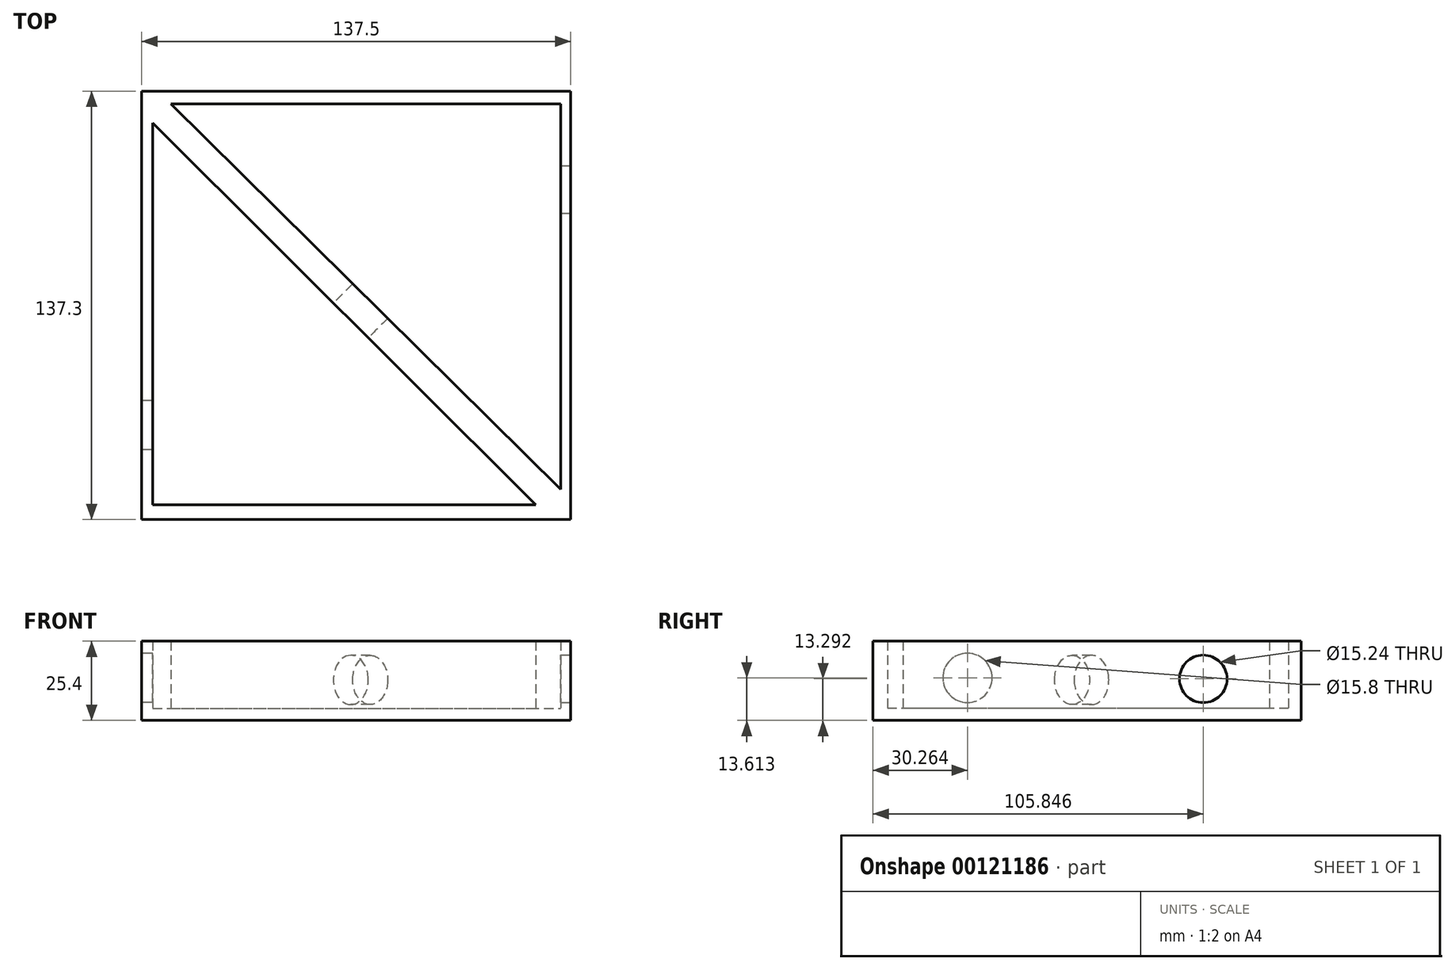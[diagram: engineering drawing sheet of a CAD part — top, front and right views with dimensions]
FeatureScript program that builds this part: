
annotation { "Feature Type Name" : "Feature", "Feature Type Description" : "" }
export const myFeature = defineFeature(function(context is Context, id is Id, definition is map)
    precondition{}
    {
        {
            var Q0;
            Q0=qCreatedBy(makeId("Top.planeOp"),FACE);
            var sketch = newSketch(context, id + "F0", { "sketchPlane" : qUnion([Q0])});
            skLineSegment(sketch, "E0.bottom", {"start": v(-66.4, 69.43) * mm, "end": v(71.1, 69.43) * mm});
            skLineSegment(sketch, "E0.top", {"start": v(-66.4, -67.87) * mm, "end": v(71.1, -67.87) * mm});
            skLineSegment(sketch, "E0.left", {"start": v(-66.4, 69.43) * mm, "end": v(-66.4, -67.87) * mm});
            skLineSegment(sketch, "E0.right", {"start": v(71.1, 69.43) * mm, "end": v(71.1, -67.87) * mm});
            skLineSegment(sketch, "E1.bottom", {"start": v(-62.87, 65.32) * mm, "end": v(67.96, 65.32) * mm});
            skLineSegment(sketch, "E1.top", {"start": v(-62.87, -63.17) * mm, "end": v(67.96, -63.17) * mm});
            skLineSegment(sketch, "E1.left", {"start": v(-62.87, 65.32) * mm, "end": v(-62.87, -63.17) * mm});
            skLineSegment(sketch, "E1.right", {"start": v(67.96, 65.32) * mm, "end": v(67.96, -63.17) * mm});
            skLineSegment(sketch, "E2", {"start": v(-62.87, 59.25) * mm, "end": v(59.93, -63.17) * mm});
            skLineSegment(sketch, "E3", {"start": v(-57, 65.32) * mm, "end": v(67.96, -58.27) * mm});
            skSolve(sketch);
        }
        {
            var Q0;
            Q0=makeQuery(id+"F0.imprint","IMPRINT",FACE,{"disambiguationData":[TD([[makeQuery(id+"F0.imprint","IMPRINT",EDGE,{"derivedFrom":sQuery(id+"F0.wireOp",EDGE,"E0.bottom")}),-1.0]])]});
            var Q1;
            {var subQ7=sQuery(id+"F0.wireOp",EDGE,"E2");Q1=makeQuery(id+"F0.imprint","IMPRINT",FACE,{"disambiguationData":[TD([[makeQuery(id+"F0.imprint","IMPRINT",EDGE,{"derivedFrom":subQ7}),1.0]])]});}
            extrude(context, id + "F1", {"entities" : qUnion([Q0, Q1]), "depth" : 25.4 * mm});
        }
        {
            var Q0;
            {var subQ3=sQuery(id+"F0.wireOp",EDGE,"E3");Q0=makeQuery(id+"F0.imprint","IMPRINT",FACE,{"disambiguationData":[TD([[makeQuery(id+"F0.imprint","IMPRINT",EDGE,{"derivedFrom":subQ3}),1.0]])]});}
            extrude(context, id + "F2", {"entities" : qUnion([Q0]), "operationType" : NewBodyOperationType.ADD, "depth" : 3.8 * mm});
        }
        {
            var Q0;
            {var subQ3=sQuery(id+"F0.wireOp",EDGE,"E2");Q0=makeQuery(id+"F0.imprint","IMPRINT",FACE,{"disambiguationData":[TD([[makeQuery(id+"F0.imprint","IMPRINT",EDGE,{"derivedFrom":subQ3}),-1.0]])]});}
            extrude(context, id + "F3", {"entities" : qUnion([Q0]), "operationType" : NewBodyOperationType.ADD, "depth" : 3.8 * mm});
        }
        {
            var Q0;
            Q0=makeQuery(id+"F1.opExtrude","SWEPT_FACE",FACE,{"disambiguationData":[OSD([sQuery(id+"F0.wireOp",EDGE,"E0.right")])]});
            var sketch = newSketch(context, id + "F4", { "sketchPlane" : qUnion([Q0])});
            skCircle(sketch, "E4", {"center": v(37.98, 13.3) * mm, "radius": 7.63 * mm});
            skSolve(sketch);
        }
        {
            var Q0;
            Q0=sQuery(id+"F4.wireOp",VERTEX,"E4.center");
            var Q1;
            Q1=makeQuery(id+"F1.opExtrude","SWEPT_BODY",BODY,{"disambiguationData":[OSD([sQuery(id+"F0.wireOp",EDGE,"E0.bottom"),sQuery(id+"F0.wireOp",EDGE,"E0.top"),sQuery(id+"F0.wireOp",EDGE,"E0.left"),sQuery(id+"F0.wireOp",EDGE,"E0.right"),sQuery(id+"F0.wireOp",EDGE,"E1.bottom"),sQuery(id+"F0.wireOp",EDGE,"E1.top"),sQuery(id+"F0.wireOp",EDGE,"E1.left"),sQuery(id+"F0.wireOp",EDGE,"E1.right"),sQuery(id+"F0.wireOp",EDGE,"E2"),sQuery(id+"F0.wireOp",EDGE,"E3")])]});
            hole(context, id + "F5", {"style" : HoleStyle.SIMPLE, "endStyle" : HoleEndStyle.BLIND, "holeDiameter" : 15.24 * mm, "holeDepth" : 12.7 * mm, "locations" : qUnion([Q0]), "scope" : qUnion([Q1])});
        }
        {
            var Q0;
            Q0=makeQuery(id+"F1.opExtrude","SWEPT_FACE",FACE,{"disambiguationData":[OSD([sQuery(id+"F0.wireOp",EDGE,"E0.left")])]});
            var sketch = newSketch(context, id + "F6", { "sketchPlane" : qUnion([Q0])});
            skCircle(sketch, "E5", {"center": v(37.6, 13.61) * mm, "radius": 7.9 * mm});
            skSolve(sketch);
        }
        {
            var Q0;
            Q0=sQuery(id+"F6.wireOp",VERTEX,"E5.center");
            var Q1;
            Q1=makeQuery(id+"F1.opExtrude","SWEPT_BODY",BODY,{"disambiguationData":[OSD([sQuery(id+"F0.wireOp",EDGE,"E0.bottom"),sQuery(id+"F0.wireOp",EDGE,"E0.top"),sQuery(id+"F0.wireOp",EDGE,"E0.left"),sQuery(id+"F0.wireOp",EDGE,"E0.right"),sQuery(id+"F0.wireOp",EDGE,"E1.bottom"),sQuery(id+"F0.wireOp",EDGE,"E1.top"),sQuery(id+"F0.wireOp",EDGE,"E1.left"),sQuery(id+"F0.wireOp",EDGE,"E1.right"),sQuery(id+"F0.wireOp",EDGE,"E2"),sQuery(id+"F0.wireOp",EDGE,"E3")])]});
            hole(context, id + "F7", {"style" : HoleStyle.SIMPLE, "endStyle" : HoleEndStyle.BLIND, "holeDiameter" : 15.8 * mm, "holeDepth" : 12.7 * mm, "locations" : qUnion([Q0]), "scope" : qUnion([Q1])});
        }
        {
            var Q0;
            Q0=makeQuery(id+"F1.opExtrude","SWEPT_FACE",FACE,{"disambiguationData":[OSD([sQuery(id+"F0.wireOp",EDGE,"E2")])]});
            var sketch = newSketch(context, id + "F8", { "sketchPlane" : qUnion([Q0])});
            skCircle(sketch, "E6", {"center": v(3.33, 12.94) * mm, "radius": 8.33 * mm});
            skSolve(sketch);
        }
        {
            var Q0;
            Q0=sQuery(id+"F8.wireOp",VERTEX,"E6.center");
            var Q1;
            Q1=makeQuery(id+"F1.opExtrude","SWEPT_BODY",BODY,{"disambiguationData":[OSD([sQuery(id+"F0.wireOp",EDGE,"E0.bottom"),sQuery(id+"F0.wireOp",EDGE,"E0.top"),sQuery(id+"F0.wireOp",EDGE,"E0.left"),sQuery(id+"F0.wireOp",EDGE,"E0.right"),sQuery(id+"F0.wireOp",EDGE,"E1.bottom"),sQuery(id+"F0.wireOp",EDGE,"E1.top"),sQuery(id+"F0.wireOp",EDGE,"E1.left"),sQuery(id+"F0.wireOp",EDGE,"E1.right"),sQuery(id+"F0.wireOp",EDGE,"E2"),sQuery(id+"F0.wireOp",EDGE,"E3")])]});
            hole(context, id + "F9", {"style" : HoleStyle.SIMPLE, "endStyle" : HoleEndStyle.BLIND, "holeDiameter" : 15.8 * mm, "holeDepth" : 12.7 * mm, "locations" : qUnion([Q0]), "scope" : qUnion([Q1])});
        }
    });
